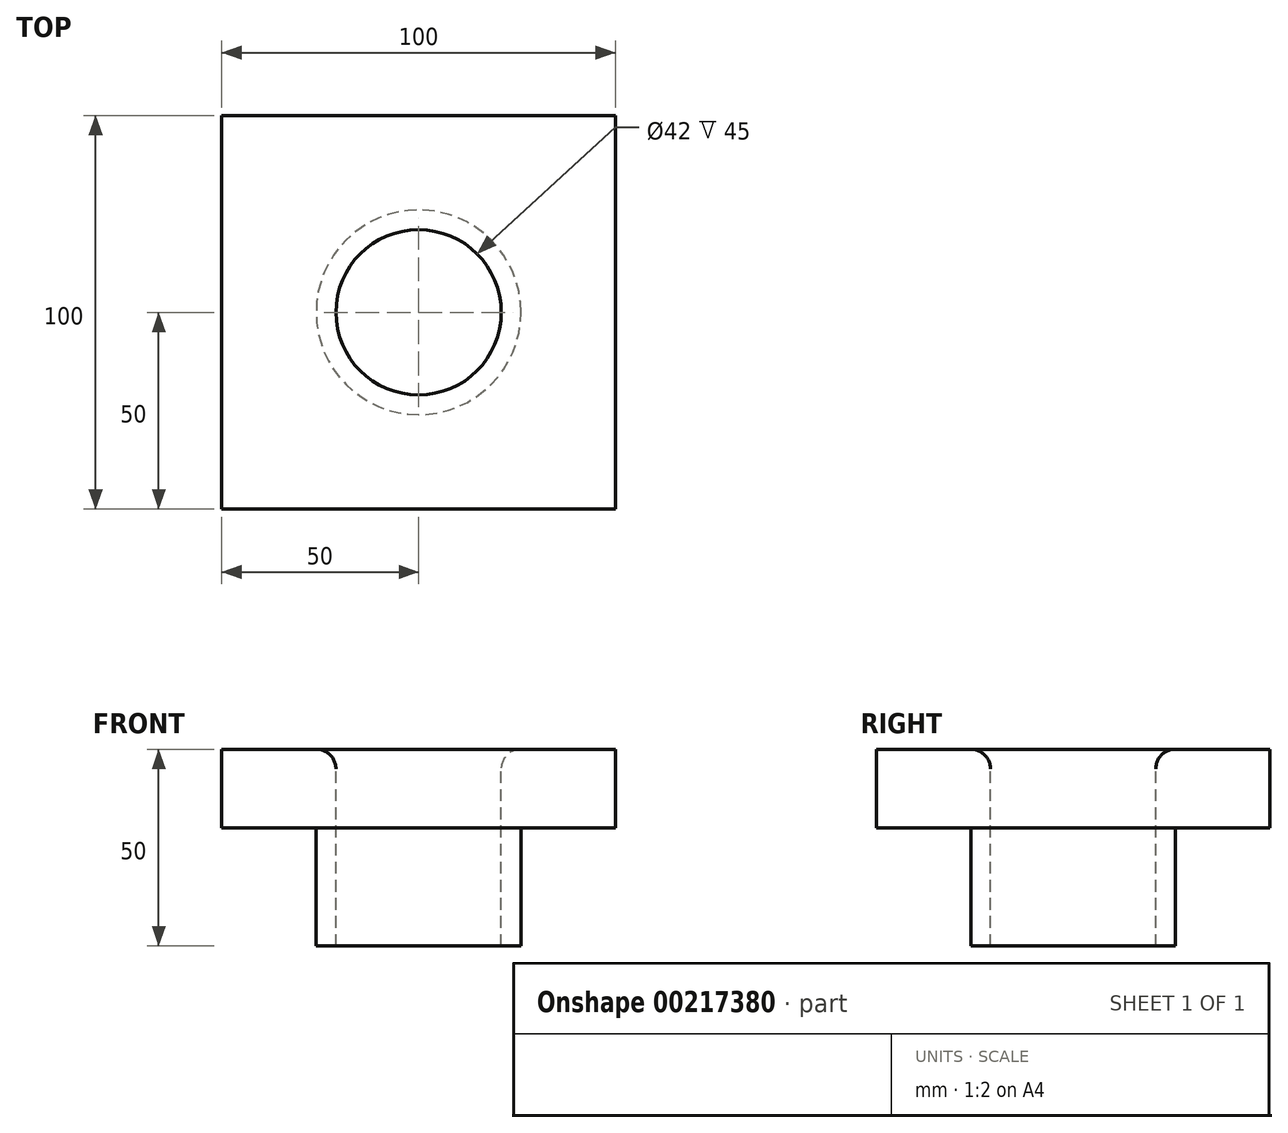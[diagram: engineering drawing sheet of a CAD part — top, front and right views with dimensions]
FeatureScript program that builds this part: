
annotation { "Feature Type Name" : "Feature", "Feature Type Description" : "" }
export const myFeature = defineFeature(function(context is Context, id is Id, definition is map)
    precondition{}
    {
        {
            var Q0;
            Q0=qCreatedBy(makeId("Front.planeOp"),FACE);
            var sketch = newSketch(context, id + "F0", { "sketchPlane" : qUnion([Q0])});
            skLineSegment(sketch, "E0", {"start": v(41, 0) * mm, "end": v(41, -5) * mm});
            skLineSegment(sketch, "E1", {"start": v(41, -5) * mm, "end": v(31, -5) * mm});
            skLineSegment(sketch, "E2", {"start": v(26, -10) * mm, "end": v(26, -50) * mm});
            skLineSegment(sketch, "E3", {"start": v(0, 0) * mm, "end": v(0, -50.07) * mm, "construction": true});
            skLineSegment(sketch, "E4", {"start": v(41, 0) * mm, "end": v(26, 0) * mm});
            skLineSegment(sketch, "E5", {"start": v(21, -5) * mm, "end": v(21, -50) * mm});
            skLineSegment(sketch, "E6", {"start": v(21, -50) * mm, "end": v(26, -50) * mm});
            skPoint(sketch, "E7.visualSharp", {"position": v(21, 0) * mm});
            skArc(sketch, "E7.filletArc", {"start": v(26, 0) * mm, "mid": v(22.46, -1.46) * mm, "end": v(21, -5) * mm});
            skArc(sketch, "E8.filletArc", {"start": v(31, -5) * mm, "mid": v(27.46, -6.46) * mm, "end": v(26, -10) * mm});
            skSolve(sketch);
        }
        {
            var Q0;
            Q0=makeQuery(id+"F0.imprint","IMPRINT",FACE,{"disambiguationData":[TD([[makeQuery(id+"F0.imprint","IMPRINT",EDGE,{"derivedFrom":sQuery(id+"F0.wireOp",EDGE,"E0")}),-1.0]])]});
            var Q1;
            Q1=sQuery(id+"F0.wireOp",EDGE,"E3");
            revolve(context, id + "F1", {"entities" : qUnion([Q0]), "axis" : qUnion([Q1]), "revolveType" : RevolveType.FULL});
        }
        {
            var Q0;
            Q0=makeQuery(id+"F1.opRevolve","SWEPT_FACE",FACE,{"disambiguationData":[OSD([sQuery(id+"F0.wireOp",EDGE,"E4")])]});
            var sketch = newSketch(context, id + "F2", { "sketchPlane" : qUnion([Q0])});
            skLineSegment(sketch, "E9.bottom", {"start": v(-50, 50) * mm, "end": v(50, 50) * mm});
            skLineSegment(sketch, "E9.top", {"start": v(-50, -50) * mm, "end": v(50, -50) * mm});
            skLineSegment(sketch, "E9.left", {"start": v(-50, 50) * mm, "end": v(-50, -50) * mm});
            skLineSegment(sketch, "E9.right", {"start": v(50, 50) * mm, "end": v(50, -50) * mm});
            skPoint(sketch, "E9.middle", {"position": v(0, 0) * mm});
            skCircle(sketch, "E10", {"center": v(0, 0) * mm, "radius": 26 * mm});
            skSolve(sketch);
        }
        {
            var Q0;
            Q0=makeQuery(id+"F2.imprint","IMPRINT",FACE,{"disambiguationData":[TD([[makeQuery(id+"F2.imprint","IMPRINT",EDGE,{"derivedFrom":sQuery(id+"F2.wireOp",EDGE,"E9.bottom")}),-1.0]])]});
            var Q1;
            Q1=makeQuery(id+"F2.imprint","IMPRINT",FACE,{"disambiguationData":[TD([[makeQuery(id+"F2.imprint","IMPRINT",EDGE,{"derivedFrom":sQuery(id+"F2.wireOp",EDGE,"E10")}),-1.0]])]});
            extrude(context, id + "F3", {"entities" : qUnion([Q0, Q1]), "operationType" : NewBodyOperationType.ADD, "oppositeDirection" : true, "depth" : 20 * mm});
        }
    });
